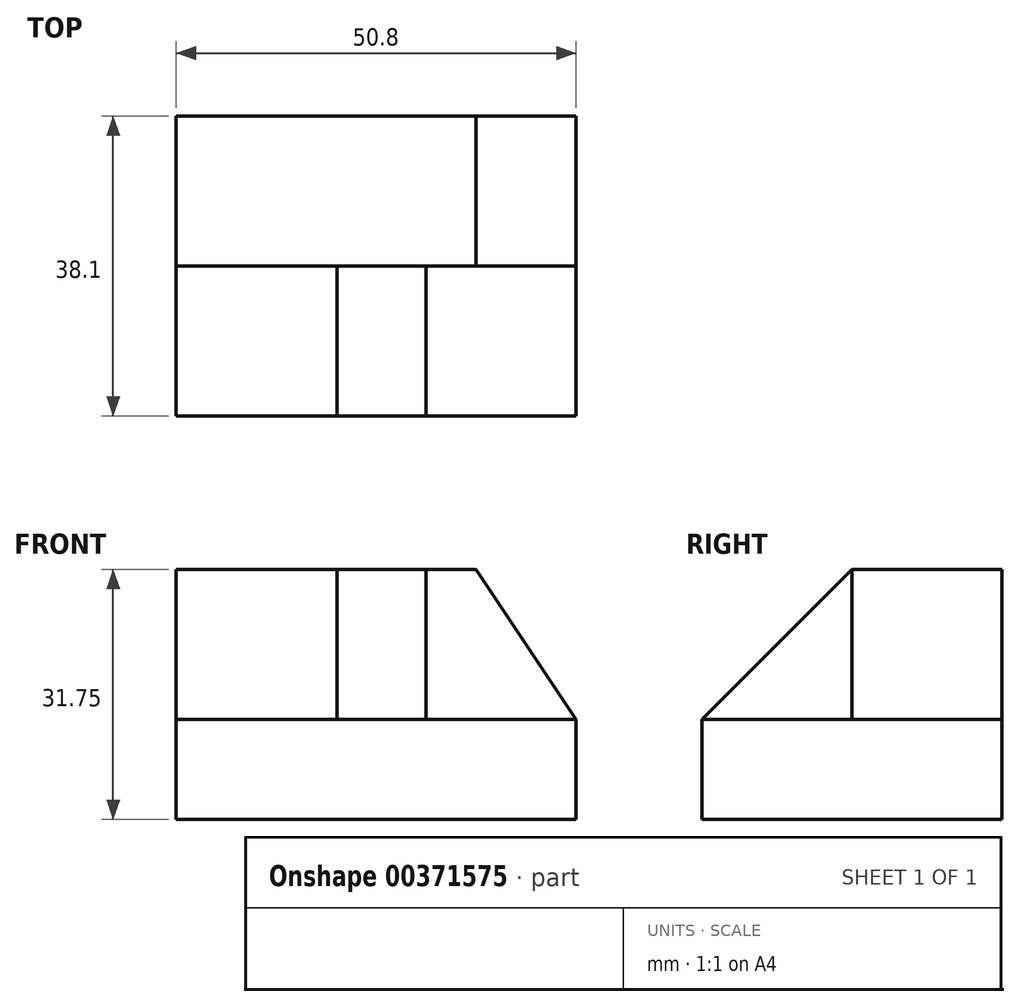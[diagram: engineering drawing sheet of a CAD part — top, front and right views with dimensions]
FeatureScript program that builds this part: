
annotation { "Feature Type Name" : "Feature", "Feature Type Description" : "" }
export const myFeature = defineFeature(function(context is Context, id is Id, definition is map)
    precondition{}
    {
        {
            var Q0;
            Q0=qCreatedBy(makeId("Front.planeOp"),FACE);
            var sketch = newSketch(context, id + "F0", { "sketchPlane" : qUnion([Q0])});
            skLineSegment(sketch, "E0", {"start": v(0, 0) * mm, "end": v(0, -31.75) * mm});
            skLineSegment(sketch, "E1", {"start": v(0, -31.75) * mm, "end": v(50.8, -31.75) * mm});
            skLineSegment(sketch, "E2", {"start": v(50.8, -31.75) * mm, "end": v(50.8, 0) * mm});
            skLineSegment(sketch, "E3", {"start": v(50.8, 0) * mm, "end": v(0, 0) * mm});
            skSolve(sketch);
        }
        {
            var Q0;
            Q0 = qSketchRegion(id + "F0", true);
            extrude(context, id + "F1", {"entities" : qUnion([Q0]), "depth" : 38.1 * mm});
        }
        {
            var Q0;
            Q0=makeQuery(id+"F1.opExtrude","SWEPT_FACE",FACE,{"disambiguationData":[OSD([sQuery(id+"F0.wireOp",EDGE,"E3")])]});
            var sketch = newSketch(context, id + "F2", { "sketchPlane" : qUnion([Q0])});
            skLineSegment(sketch, "E4", {"start": v(50.8, -19.05) * mm, "end": v(31.75, -19.05) * mm});
            skLineSegment(sketch, "E5", {"start": v(31.75, -19.05) * mm, "end": v(31.75, -38.1) * mm});
            skLineSegment(sketch, "E6", {"start": v(31.75, -38.1) * mm, "end": v(50.8, -38.1) * mm});
            skLineSegment(sketch, "E7", {"start": v(50.8, -38.1) * mm, "end": v(50.8, -19.05) * mm});
            skSolve(sketch);
        }
        {
            var Q0;
            Q0 = qSketchRegion(id + "F2", true);
            extrude(context, id + "F3", {"entities" : qUnion([Q0]), "operationType" : NewBodyOperationType.REMOVE, "oppositeDirection" : true, "depth" : 19.05 * mm});
        }
        {
            var Q0;
            Q0=makeQuery(id+"F1.opExtrude","SWEPT_FACE",FACE,{"disambiguationData":[OSD([sQuery(id+"F0.wireOp",EDGE,"E3")])]});
            var sketch = newSketch(context, id + "F4", { "sketchPlane" : qUnion([Q0])});
            skLineSegment(sketch, "E8", {"start": v(0, -19.05) * mm, "end": v(20.43, -19.05) * mm});
            skPoint(sketch, "E8.endSnap0", {"position": v(0, -19.05) * mm});
            skLineSegment(sketch, "E9", {"start": v(20.43, -19.05) * mm, "end": v(20.43, -38.1) * mm});
            skLineSegment(sketch, "E10", {"start": v(20.43, -38.1) * mm, "end": v(0, -38.1) * mm});
            skLineSegment(sketch, "E11", {"start": v(0, -38.1) * mm, "end": v(0, -19.05) * mm});
            skSolve(sketch);
        }
        {
            var Q0;
            Q0 = qSketchRegion(id + "F4", true);
            extrude(context, id + "F5", {"entities" : qUnion([Q0]), "operationType" : NewBodyOperationType.REMOVE, "oppositeDirection" : true, "depth" : 19.05 * mm});
        }
        {
            var Q0;
            Q0=makeQuery(id+"F3.boolean.opBoolean","COPY",FACE,{"derivedFrom":makeQuery(id+"F3.opExtrude","SWEPT_FACE",FACE,{"disambiguationData":[OSD([sQuery(id+"F2.wireOp",EDGE,"E5")])]})});
            var sketch = newSketch(context, id + "F6", { "sketchPlane" : qUnion([Q0])});
            skLineSegment(sketch, "E12", {"start": v(-19.05, 0) * mm, "end": v(-38.1, -19.05) * mm});
            skLineSegment(sketch, "E13", {"start": v(-19.05, 0) * mm, "end": v(-38.1, 0) * mm});
            skLineSegment(sketch, "E14", {"start": v(-38.1, 0) * mm, "end": v(-38.1, -19.05) * mm});
            skSolve(sketch);
        }
        {
            var Q0;
            Q0 = qSketchRegion(id + "F6", true);
            extrude(context, id + "F7", {"entities" : qUnion([Q0]), "operationType" : NewBodyOperationType.REMOVE, "oppositeDirection" : true, "depth" : 25.4 * mm});
        }
        {
            var Q0;
            Q0=makeQuery(id+"F3.boolean.opBoolean","COPY",FACE,{"derivedFrom":makeQuery(id+"F3.opExtrude","SWEPT_FACE",FACE,{"disambiguationData":[OSD([sQuery(id+"F2.wireOp",EDGE,"E4")])]})});
            var sketch = newSketch(context, id + "F8", { "sketchPlane" : qUnion([Q0])});
            skLineSegment(sketch, "E15", {"start": v(38.1, 0) * mm, "end": v(50.8, -19.05) * mm});
            skLineSegment(sketch, "E16", {"start": v(50.8, -19.05) * mm, "end": v(50.8, 0) * mm});
            skLineSegment(sketch, "E17", {"start": v(50.8, 0) * mm, "end": v(38.1, 0) * mm});
            skSolve(sketch);
        }
        {
            var Q0;
            Q0 = qSketchRegion(id + "F8", true);
            extrude(context, id + "F9", {"entities" : qUnion([Q0]), "operationType" : NewBodyOperationType.REMOVE, "oppositeDirection" : true, "depth" : 25.4 * mm});
        }
    });
